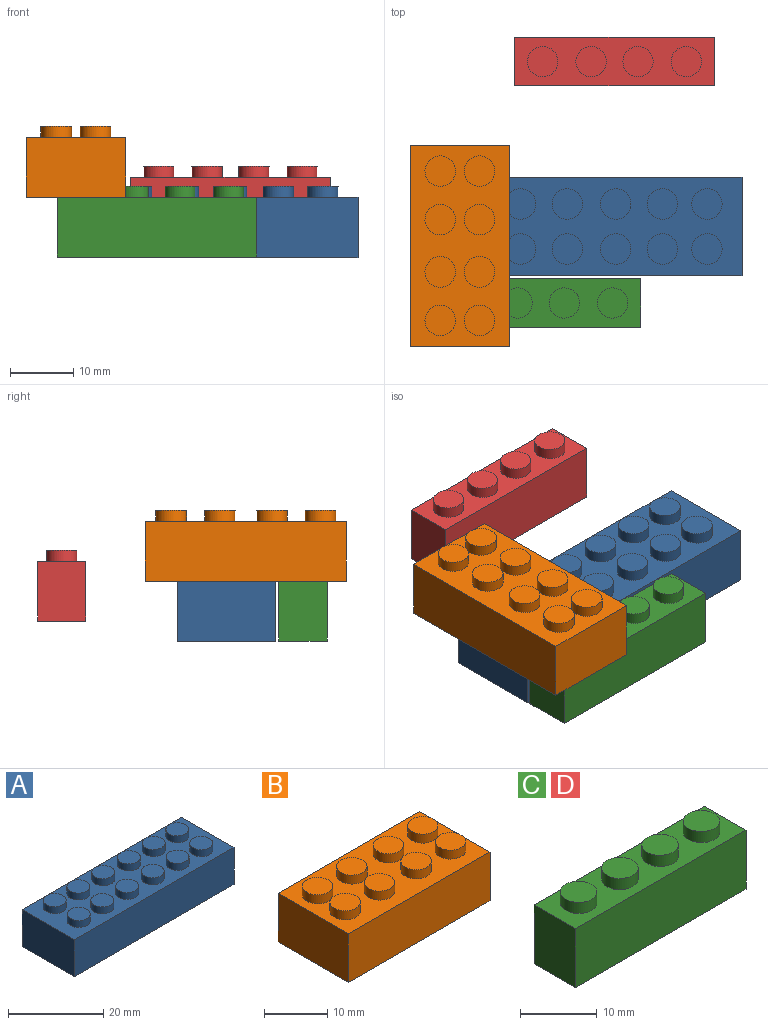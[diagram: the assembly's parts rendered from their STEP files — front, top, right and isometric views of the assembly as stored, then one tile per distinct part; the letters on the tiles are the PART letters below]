
ASSEMBLY  parts=4 mates=2
PART A: 30 faces, bbox 47.5x15.5x11.3 mm
  f0: plane 15.49x9.5mm, normal (-1,0,0), area 147.2mm2, adj f1,f3,f4,f5
  f1: plane 47.5x9.5mm, normal (0,-1,0), area 451.2mm2, adj f0,f2,f4,f5
  f2: plane 15.49x9.5mm, normal (1,0,0), area 147.2mm2, adj f1,f3,f4,f5
  f3: plane 47.5x9.5mm, normal (0,1,0), area 451.2mm2, adj f0,f2,f4,f5
  f4: plane 47.5x15.49mm, normal (0,0,1), area 516.4mm2, adj f0,f1,f2,f3,f6,f8,f10,f12
  f5: plane 47.5x15.49mm, normal (0,0,-1), area 735.9mm2, adj f0,f1,f2,f3
  f6: cylinder r=2.41mm len=4.83mm, axis (0,0,-1), area 27mm2, adj f4,f7
  f7: plane 4.83x4.83mm, normal (0,0,1), area 18.3mm2, adj f6
  f8: cylinder r=2.41mm len=4.83mm, axis (0,0,-1), area 27mm2, adj f4,f9
  f9: plane 4.83x4.83mm, normal (0,0,1), area 18.3mm2, adj f8
  f10: cylinder r=2.41mm len=4.83mm, axis (0,0,-1), area 27mm2, adj f4,f11
  f11: plane 4.83x4.83mm, normal (0,0,1), area 18.3mm2, adj f10
  f12: cylinder r=2.41mm len=4.83mm, axis (0,0,-1), area 27mm2, adj f4,f13
  f13: plane 4.83x4.83mm, normal (0,0,1), area 18.3mm2, adj f12
  f14: cylinder r=2.41mm len=4.83mm, axis (0,0,-1), area 27mm2, adj f4,f15
  f15: plane 4.83x4.83mm, normal (0,0,1), area 18.3mm2, adj f14
  f16: cylinder r=2.41mm len=4.83mm, axis (0,0,-1), area 27mm2, adj f4,f17
  f17: plane 4.83x4.83mm, normal (0,0,1), area 18.3mm2, adj f16
  f18: cylinder r=2.41mm len=4.83mm, axis (0,0,-1), area 27mm2, adj f4,f19
  f19: plane 4.83x4.83mm, normal (0,0,1), area 18.3mm2, adj f18
  f20: cylinder r=2.41mm len=4.83mm, axis (0,0,-1), area 27mm2, adj f4,f21
  f21: plane 4.83x4.83mm, normal (0,0,1), area 18.3mm2, adj f20
  f22: cylinder r=2.41mm len=4.83mm, axis (0,0,-1), area 27mm2, adj f4,f23
  f23: plane 4.83x4.83mm, normal (0,0,1), area 18.3mm2, adj f22
  f24: cylinder r=2.41mm len=4.83mm, axis (0,0,-1), area 27mm2, adj f4,f25
  f25: plane 4.83x4.83mm, normal (0,0,1), area 18.3mm2, adj f24
  f26: cylinder r=2.41mm len=4.83mm, axis (0,0,-1), area 27mm2, adj f4,f27
  f27: plane 4.83x4.83mm, normal (0,0,1), area 18.3mm2, adj f26
  f28: cylinder r=2.41mm len=4.83mm, axis (0,0,-1), area 27mm2, adj f4,f29
  f29: plane 4.83x4.83mm, normal (0,0,1), area 18.3mm2, adj f28
PART B: 22 faces, bbox 31.8x15.7x11.2 mm
  f0: plane 31.75x9.45mm, normal (0,-1,0), area 300mm2, adj f1,f3,f4,f5
  f1: plane 15.75x9.45mm, normal (1,0,0), area 148.8mm2, adj f0,f2,f4,f5
  f2: plane 31.75x9.45mm, normal (0,1,0), area 300mm2, adj f1,f3,f4,f5
  f3: plane 15.75x9.45mm, normal (-1,0,0), area 148.8mm2, adj f0,f2,f4,f5
  f4: plane 31.75x15.75mm, normal (0,0,1), area 353.7mm2, adj f0,f1,f2,f3,f6,f8,f10,f12
  f5: plane 31.75x15.75mm, normal (0,0,-1), area 500mm2, adj f0,f1,f2,f3
  f6: cylinder r=2.41mm len=4.83mm, axis (0,0,-1), area 26.2mm2, adj f4,f7
  f7: plane 4.83x4.83mm, normal (0,0,1), area 18.3mm2, adj f6
  f8: cylinder r=2.41mm len=4.83mm, axis (0,0,-1), area 26.2mm2, adj f4,f9
  f9: plane 4.83x4.83mm, normal (0,0,1), area 18.3mm2, adj f8
  f10: cylinder r=2.41mm len=4.83mm, axis (0,0,-1), area 26.2mm2, adj f4,f11
  f11: plane 4.83x4.83mm, normal (0,0,1), area 18.3mm2, adj f10
  f12: cylinder r=2.41mm len=4.83mm, axis (0,0,-1), area 26.2mm2, adj f4,f13
  f13: plane 4.83x4.83mm, normal (0,0,1), area 18.3mm2, adj f12
  f14: cylinder r=2.41mm len=4.83mm, axis (0,0,-1), area 26.2mm2, adj f4,f15
  f15: plane 4.83x4.83mm, normal (0,0,1), area 18.3mm2, adj f14
  f16: cylinder r=2.41mm len=4.83mm, axis (0,0,-1), area 26.2mm2, adj f4,f17
  f17: plane 4.83x4.83mm, normal (0,0,1), area 18.3mm2, adj f16
  f18: cylinder r=2.41mm len=4.83mm, axis (0,0,-1), area 26.2mm2, adj f4,f19
  f19: plane 4.83x4.83mm, normal (0,0,1), area 18.3mm2, adj f18
  f20: cylinder r=2.41mm len=4.83mm, axis (0,0,-1), area 26.2mm2, adj f4,f21
  f21: plane 4.83x4.83mm, normal (0,0,1), area 18.3mm2, adj f20
PART C: 14 faces, bbox 31.5x7.6x11.2 mm
  f0: plane 9.42x7.62mm, normal (-1,0,0), area 71.8mm2, adj f1,f3,f4,f5
  f1: plane 31.5x9.42mm, normal (0,-1,0), area 296.8mm2, adj f0,f2,f4,f5
  f2: plane 9.42x7.62mm, normal (1,0,0), area 71.8mm2, adj f1,f3,f4,f5
  f3: plane 31.5x9.42mm, normal (0,1,0), area 296.8mm2, adj f0,f2,f4,f5
  f4: plane 31.5x7.62mm, normal (0,0,1), area 168.4mm2, adj f0,f1,f2,f3,f6,f8,f10,f12
  f5: plane 31.5x7.62mm, normal (0,0,-1), area 240mm2, adj f0,f1,f2,f3
  f6: cylinder r=2.39mm len=4.78mm, axis (0,0,-1), area 26.7mm2, adj f4,f7
  f7: plane 4.78x4.78mm, normal (0,0,1), area 17.9mm2, adj f6
  f8: cylinder r=2.39mm len=4.78mm, axis (0,0,-1), area 26.7mm2, adj f4,f9
  f9: plane 4.78x4.78mm, normal (0,0,1), area 17.9mm2, adj f8
  f10: cylinder r=2.39mm len=4.78mm, axis (0,0,-1), area 26.7mm2, adj f4,f11
  f11: plane 4.78x4.78mm, normal (0,0,1), area 17.9mm2, adj f10
  f12: cylinder r=2.39mm len=4.78mm, axis (0,0,-1), area 26.7mm2, adj f4,f13
  f13: plane 4.78x4.78mm, normal (0,0,1), area 17.9mm2, adj f12
PART D: same geometry as C
PLACE A t=(-14.33,-9.18,-7.36)mm
PLACE B rot(axis=(0,0,-1),90deg) t=(-35.1,-12.24,6.87)mm
PLACE C t=(-22.33,-21.25,-7.28)mm
PLACE D t=(-10.7,16.83,-4.13)mm
MATE planar C.f4 <-> B.f5  axis (0,0,1) through (-38.08,-25.06,2.14)mm
MATE planar B.f5 <-> A.f4  axis (0,0,-1) through (-42.97,-12.24,2.14)mm
